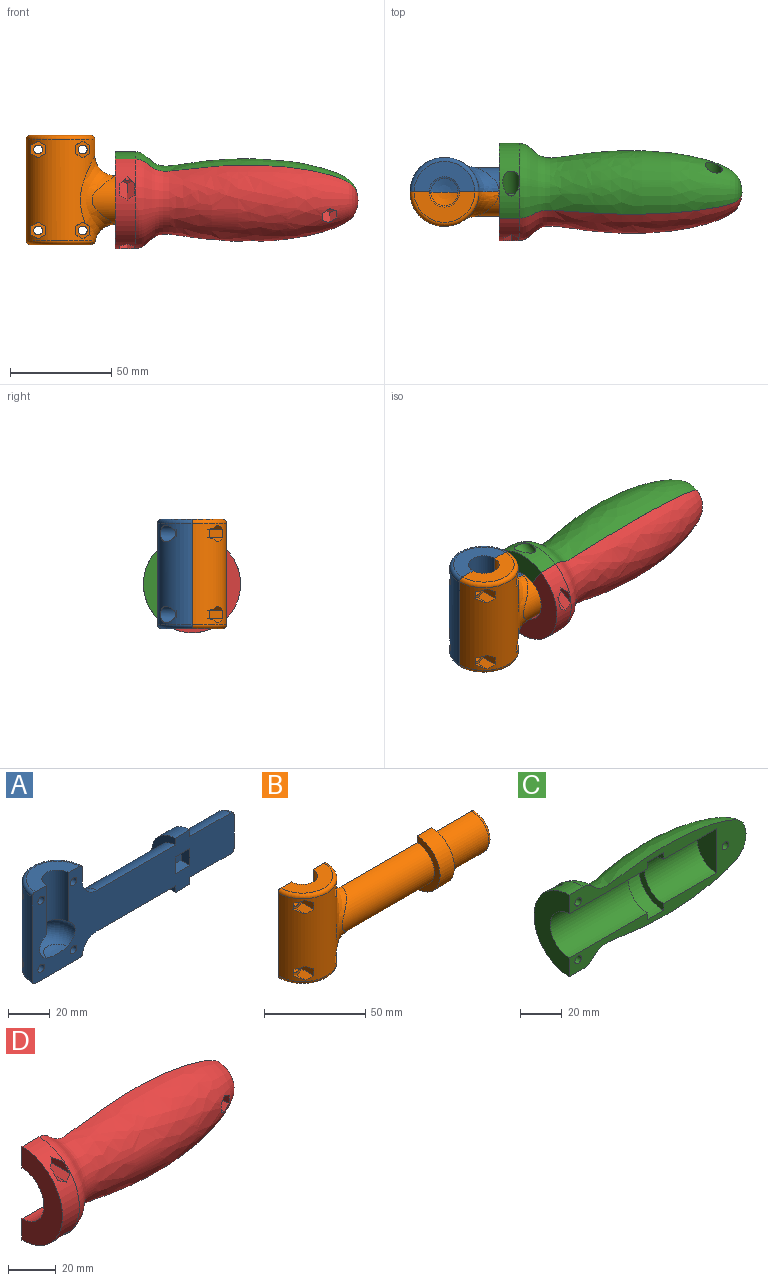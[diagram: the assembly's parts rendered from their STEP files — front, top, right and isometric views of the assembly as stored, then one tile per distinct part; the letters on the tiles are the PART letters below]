
ASSEMBLY  parts=4 mates=3
PART A: 35 faces, bbox 139.5x21.6x55.1 mm
  f0: cylinder r=17mm len=50mm, axis (0,0,1), area 1879.9mm2, adj f2,f12,f19,f20,f22,f23,f24,f25
  f1: cylinder r=2.2mm len=6mm, axis (0,-1,0), area 82.9mm2, adj f12,f28
  f2: bspline ~44.05x17.18mm, area 505.6mm2, adj f0,f11,f12,f18,f25
  f3: cylinder r=2.2mm len=6mm, axis (0,-1,0), area 82.9mm2, adj f12,f29
  f4: cylinder r=2.2mm len=6mm, axis (0,-1,0), area 82.9mm2, adj f12,f26
  f5: cylinder r=2.2mm len=6mm, axis (0,-1,0), area 82.9mm2, adj f12,f27
  f6: plane 20x10mm, normal (1,0,0), area 157.1mm2, adj f12,f21
  f7: cylinder r=12mm len=28mm, axis (-1,0,0), area 1055.6mm2, adj f8,f12,f21
  f8: plane 32x16mm, normal (1,0,0), area 175.9mm2, adj f7,f9,f12
  f9: cylinder r=16mm len=32mm, axis (-1,0,0), area 502.7mm2, adj f8,f10,f12
  f10: plane 32x16mm, normal (-1,0,0), area 175.9mm2, adj f9,f11,f12
  f11: cylinder r=12mm len=53mm, axis (-1,0,0), area 1998.1mm2, adj f2,f10,f12
  f12: plane 138.09x55.09mm, normal (0,-1,0), area 3522.4mm2, adj f0,f1,f2,f3,f4,f5,f6,f7
  f13: plane 30.17x15mm, normal (0,0,-1), area 353.9mm2, adj f12,f18,f19
  f14: plane 30x15mm, normal (0,0,1), area 265.1mm2, adj f12,f17,f20
  f15: sphere r=23mm, area 69.8mm2, adj f12,f16
  f16: torus R=4.53mm, axis (0,0,1), area 587.6mm2, adj f12,f15,f17
  f17: cylinder r=7.5mm len=29mm, axis (0,0,1), area 683.3mm2, adj f12,f14,f16
  f18: bspline ~9.18x3.75mm, area 16.5mm2, adj f2,f12,f13,f19
  f19: torus R=15mm, axis (0,0,-1), area 142.9mm2, adj f0,f12,f13,f18
  f20: torus R=15mm, axis (0,0,1), area 160.6mm2, adj f0,f12,f14
  f21: torus R=10mm, axis (1,0,0), area 111.3mm2, adj f6,f7,f12
  f22: cylinder r=4mm len=8mm, axis (0,1,0), area 115mm2, adj f0,f27
  f23: cylinder r=4mm len=8mm, axis (0,1,0), area 115mm2, adj f0,f26
  f24: cylinder r=4mm len=8mm, axis (0,1,0), area 115mm2, adj f0,f29
  f25: cylinder r=4mm len=8mm, axis (0,1,0), area 117.1mm2, adj f0,f2,f28
  f26: cone r=2.2mm half-angle=45deg, axis (0,1,0), area 49.6mm2, adj f4,f23
  f27: cone r=2.2mm half-angle=45deg, axis (0,1,0), area 49.6mm2, adj f5,f22
  f28: cone r=2.2mm half-angle=45deg, axis (0,1,0), area 49.6mm2, adj f1,f25
  f29: cone r=2.2mm half-angle=45deg, axis (0,1,0), area 49.6mm2, adj f3,f24
  f30: plane 10x6mm, normal (1,0,0), area 60mm2, adj f12,f31,f33,f34
  f31: plane 10x6mm, normal (0,0,1), area 60mm2, adj f12,f30,f32,f34
  f32: plane 10x6mm, normal (-1,0,0), area 60mm2, adj f12,f31,f33,f34
  f33: plane 10x6mm, normal (0,0,-1), area 60mm2, adj f12,f30,f32,f34
  f34: plane 10x10mm, normal (0,-1,0), area 100mm2, adj f30,f31,f32,f33
PART B: 55 faces, bbox 139.5x20.9x55.1 mm
  f0: cylinder r=2.2mm len=7mm, axis (0,1,0), area 96.8mm2, adj f11,f23
  f1: cylinder r=2.2mm len=7mm, axis (0,1,0), area 96.8mm2, adj f11,f30
  f2: cylinder r=2.2mm len=7mm, axis (0,1,0), area 96.8mm2, adj f11,f44
  f3: cylinder r=2.2mm len=7mm, axis (0,1,0), area 96.8mm2, adj f11,f37
  f4: cylinder r=17mm len=50mm, axis (0,0,1), area 1906.5mm2, adj f11,f17,f18,f19,f20,f21,f22,f24
  f5: plane 20x10mm, normal (1,0,0), area 157.1mm2, adj f11,f49
  f6: cylinder r=12mm len=28mm, axis (-1,0,0), area 1055.6mm2, adj f7,f11,f49
  f7: plane 32x16mm, normal (1,0,0), area 175.9mm2, adj f6,f8,f11
  f8: cylinder r=16mm len=32mm, axis (-1,0,0), area 502.7mm2, adj f7,f9,f11
  f9: plane 32x16mm, normal (-1,0,0), area 175.9mm2, adj f8,f10,f11
  f10: cylinder r=12mm len=53mm, axis (-1,0,0), area 1998.1mm2, adj f9,f11,f45
  f11: plane 138.09x55.09mm, normal (0,1,0), area 3522.4mm2, adj f0,f1,f2,f3,f4,f5,f6,f7
  f12: plane 30.17x15mm, normal (0,0,-1), area 353.9mm2, adj f11,f46,f47
  f13: plane 30x15mm, normal (0,0,1), area 265.1mm2, adj f11,f16,f48
  f14: sphere r=23mm, area 69.8mm2, adj f11,f15
  f15: torus R=4.53mm, axis (0,0,1), area 587.6mm2, adj f11,f14,f16
  f16: cylinder r=7.5mm len=29mm, axis (0,0,1), area 683.3mm2, adj f11,f13,f15
  f17: plane 6.16x3.8mm, normal (-0.5,0,-0.87), area 16.9mm2, adj f4,f18,f22,f23
  f18: plane 8.39x3.69mm, normal (0.5,0,-0.87), area 30.1mm2, adj f4,f17,f19,f23
  f19: plane 8.31x4.16mm, normal (1,0,0), area 34.5mm2, adj f4,f18,f20,f23
  f20: plane 8.39x3.69mm, normal (0.5,0,0.87), area 30.1mm2, adj f4,f19,f21,f23
  f21: plane 6.16x3.8mm, normal (-0.5,0,0.87), area 16.9mm2, adj f4,f20,f22,f23
  f22: plane 4.16x1.71mm, normal (-1,0,0), area 7.1mm2, adj f4,f17,f21,f23
  f23: plane 8.31x7.2mm, normal (0,-1,0), area 29.7mm2, adj f0,f17,f18,f19,f20,f21,f22
  f24: plane 8.39x3.69mm, normal (-0.5,0,-0.87), area 30.1mm2, adj f4,f25,f29,f30
  f25: plane 6.16x3.8mm, normal (0.5,0,-0.87), area 16.9mm2, adj f4,f24,f26,f30
  f26: plane 4.16x1.71mm, normal (1,0,0), area 7.1mm2, adj f4,f25,f27,f30
  f27: plane 6.16x3.8mm, normal (0.5,0,0.87), area 16.9mm2, adj f4,f26,f28,f30
  f28: plane 8.39x3.69mm, normal (-0.5,0,0.87), area 30.1mm2, adj f4,f27,f29,f30
  f29: plane 8.31x4.16mm, normal (-1,0,0), area 34.5mm2, adj f4,f24,f28,f30
  f30: plane 8.31x7.2mm, normal (0,-1,0), area 29.7mm2, adj f1,f24,f25,f26,f27,f28,f29
  f31: plane 8.39x3.69mm, normal (-0.5,0,-0.87), area 30.1mm2, adj f4,f32,f36,f37
  f32: plane 6.16x3.8mm, normal (0.5,0,-0.87), area 16.9mm2, adj f4,f31,f33,f37
  f33: plane 4.16x1.71mm, normal (1,0,0), area 7.1mm2, adj f4,f32,f34,f37
  f34: plane 6.16x3.8mm, normal (0.5,0,0.87), area 16.9mm2, adj f4,f33,f35,f37
  f35: plane 8.39x3.69mm, normal (-0.5,0,0.87), area 30.1mm2, adj f4,f34,f36,f37
  f36: plane 8.31x4.16mm, normal (-1,0,0), area 34.5mm2, adj f4,f31,f35,f37
  f37: plane 8.31x7.2mm, normal (0,-1,0), area 29.7mm2, adj f3,f31,f32,f33,f34,f35,f36
  f38: plane 5.98x3.62mm, normal (-0.5,0,-0.87), area 17.5mm2, adj f4,f39,f43,f44,f45
  f39: plane 8.39x3.69mm, normal (0.5,0,-0.87), area 30.1mm2, adj f4,f38,f40,f44
  f40: plane 8.31x4.16mm, normal (1,0,0), area 34.5mm2, adj f4,f39,f41,f44
  f41: plane 8.39x3.69mm, normal (0.5,0,0.87), area 30.1mm2, adj f4,f40,f42,f44
  f42: plane 6.16x3.8mm, normal (-0.5,0,0.87), area 16.9mm2, adj f4,f41,f43,f44,f45
  f43: plane 4.16x2.33mm, normal (-1,0,0), area 8.1mm2, adj f38,f42,f44,f45
  f44: plane 8.31x7.2mm, normal (0,-1,0), area 29.7mm2, adj f2,f38,f39,f40,f41,f42,f43
  f45: bspline ~44.01x17.16mm, area 495.9mm2, adj f4,f10,f11,f38,f42,f43,f46
  f46: bspline ~9.18x3.75mm, area 16.5mm2, adj f11,f12,f45,f47
  f47: torus R=15mm, axis (0,0,-1), area 142.9mm2, adj f4,f11,f12,f46
  f48: torus R=15mm, axis (0,0,1), area 160.6mm2, adj f4,f11,f13
  f49: torus R=10mm, axis (1,0,0), area 111.3mm2, adj f5,f6,f11
  f50: plane 10x6mm, normal (-1,0,0), area 60mm2, adj f11,f51,f53,f54
  f51: plane 10x6mm, normal (0,0,1), area 60mm2, adj f11,f50,f52,f54
  f52: plane 10x6mm, normal (1,0,0), area 60mm2, adj f11,f51,f53,f54
  f53: plane 10x6mm, normal (0,0,-1), area 60mm2, adj f11,f50,f52,f54
  f54: plane 10x10mm, normal (0,1,0), area 100mm2, adj f50,f51,f52,f53
PART C: 19 faces, bbox 120x24x48 mm
  f0: revolved ~110x48mm, area 6482.1mm2, adj f1,f12,f13,f14,f15
  f1: cylinder r=24mm len=48mm, axis (-1,0,0), area 588.8mm2, adj f0,f5,f12,f14,f15
  f2: cylinder r=2.2mm len=5.05mm, axis (0,-1,0), area 69.8mm2, adj f12,f17
  f3: cylinder r=2.2mm len=5.05mm, axis (0,-1,0), area 69.8mm2, adj f12,f16
  f4: cylinder r=2.2mm len=5.05mm, axis (0,-1,0), area 69.8mm2, adj f12,f18
  f5: plane 48x24mm, normal (-1,0,0), area 639.3mm2, adj f1,f6,f12
  f6: cylinder r=13mm len=53mm, axis (-1,0,0), area 2164.6mm2, adj f5,f7,f12
  f7: plane 34x17mm, normal (1,0,0), area 188.5mm2, adj f6,f8,f12
  f8: cylinder r=17mm len=34mm, axis (-1,0,0), area 587.5mm2, adj f7,f9,f12
  f9: plane 34x17mm, normal (-1,0,0), area 188.5mm2, adj f8,f10,f12
  f10: cylinder r=13mm len=36mm, axis (-1,0,0), area 1470.3mm2, adj f9,f11,f12
  f11: plane 26x13mm, normal (-1,0,0), area 265.5mm2, adj f10,f12
  f12: plane 120.02x48.02mm, normal (0,-1,0), area 1711.8mm2, adj f0,f1,f2,f3,f4,f5,f6,f7
  f13: cylinder r=4.25mm len=8.91mm, axis (0,1,0), area 192.6mm2, adj f0,f18
  f14: cylinder r=4.25mm len=13.23mm, axis (0,1,0), area 247.3mm2, adj f0,f1,f17
  f15: cylinder r=4.25mm len=13.23mm, axis (0,1,0), area 247.3mm2, adj f0,f1,f16
  f16: cone r=2.15mm half-angle=45deg, axis (0,1,0), area 58.7mm2, adj f3,f15
  f17: cone r=2.15mm half-angle=45deg, axis (0,1,0), area 58.7mm2, adj f2,f14
  f18: cone r=2.15mm half-angle=45deg, axis (0,1,0), area 58.7mm2, adj f4,f13
PART D: 34 faces, bbox 120.1x24.1x48.1 mm
  f0: cylinder r=2.2mm len=5mm, axis (0,1,0), area 69.1mm2, adj f12,f26
  f1: cylinder r=2.2mm len=5mm, axis (0,1,0), area 69.1mm2, adj f12,f19
  f2: cylinder r=2.2mm len=5mm, axis (0,1,0), area 69.1mm2, adj f12,f33
  f3: revolved ~110x48mm, area 6495.4mm2, adj f4,f12,f27,f28,f29,f30,f31,f32
  f4: cylinder r=24mm len=48mm, axis (-1,0,0), area 623.4mm2, adj f3,f5,f12,f13,f14,f15,f16,f17
  f5: plane 48x24mm, normal (-1,0,0), area 639.3mm2, adj f4,f6,f12
  f6: cylinder r=13mm len=53mm, axis (-1,0,0), area 2164.6mm2, adj f5,f7,f12
  f7: plane 34x17mm, normal (1,0,0), area 188.5mm2, adj f6,f8,f12
  f8: cylinder r=17mm len=34mm, axis (-1,0,0), area 587.5mm2, adj f7,f9,f12
  f9: plane 34x17mm, normal (-1,0,0), area 188.5mm2, adj f8,f10,f12
  f10: cylinder r=13mm len=36mm, axis (-1,0,0), area 1470.3mm2, adj f9,f11,f12
  f11: plane 26x13mm, normal (-1,0,0), area 265.5mm2, adj f10,f12
  f12: plane 120.02x48.02mm, normal (0,1,0), area 1711.8mm2, adj f0,f1,f2,f3,f4,f5,f6,f7
  f13: plane 15.34x3.67mm, normal (-0.5,0,-0.87), area 60.5mm2, adj f4,f14,f18,f19
  f14: plane 15.34x3.67mm, normal (0.5,0,-0.87), area 60.5mm2, adj f4,f13,f15,f19
  f15: plane 13.8x4.16mm, normal (1,0,0), area 49.3mm2, adj f4,f14,f16,f19
  f16: plane 9.56x3.6mm, normal (0.5,0,0.87), area 33.4mm2, adj f4,f15,f17,f19
  f17: plane 9.56x3.6mm, normal (-0.5,0,0.87), area 33.4mm2, adj f4,f16,f18,f19
  f18: plane 13.8x4.16mm, normal (-1,0,0), area 49.3mm2, adj f4,f13,f17,f19
  f19: plane 8.31x7.2mm, normal (0,-1,0), area 29.7mm2, adj f1,f13,f14,f15,f16,f17,f18
  f20: plane 9.56x3.6mm, normal (-0.5,0,-0.87), area 33.4mm2, adj f4,f21,f25,f26
  f21: plane 9.56x3.6mm, normal (0.5,0,-0.87), area 33.4mm2, adj f4,f20,f22,f26
  f22: plane 13.8x4.16mm, normal (1,0,0), area 49.3mm2, adj f4,f21,f23,f26
  f23: plane 15.34x3.67mm, normal (0.5,0,0.87), area 60.5mm2, adj f4,f22,f24,f26
  f24: plane 15.34x3.67mm, normal (-0.5,0,0.87), area 60.5mm2, adj f4,f23,f25,f26
  f25: plane 13.8x4.16mm, normal (-1,0,0), area 49.3mm2, adj f4,f20,f24,f26
  f26: plane 8.31x7.2mm, normal (0,-1,0), area 29.7mm2, adj f0,f20,f21,f22,f23,f24,f25
  f27: plane 9.11x3.6mm, normal (-0.5,0,-0.87), area 36.1mm2, adj f3,f28,f32,f33
  f28: plane 10.69x3.6mm, normal (0.5,0,-0.87), area 41.3mm2, adj f3,f27,f29,f33
  f29: plane 10.83x4.16mm, normal (1,0,0), area 44.8mm2, adj f3,f28,f30,f33
  f30: plane 10.69x3.6mm, normal (0.5,0,0.87), area 41.3mm2, adj f3,f29,f31,f33
  f31: plane 9.11x3.6mm, normal (-0.5,0,0.87), area 36.1mm2, adj f3,f30,f32,f33
  f32: plane 8.36x4.16mm, normal (-1,0,0), area 34.5mm2, adj f3,f27,f31,f33
  f33: plane 8.31x7.2mm, normal (0,-1,0), area 29.7mm2, adj f2,f27,f28,f29,f30,f31,f32
PLACE A at identity
PLACE B at identity fixed
PLACE C rot(axis=(1,0,0),32.5deg) t=(27,0,0)mm
PLACE D rot(axis=(1,0,0),32.5deg) t=(27,0,0)mm
MATE fastened D.f0 <-> C.f2  axis (0,0.84,0.54) through (33,-9.14,14.33)mm
MATE revolute D.f4 <-> B.f6  axis (1,0,0) through (80,0,0)mm
MATE fastened B.f1 <-> A.f4  axis (0,1,0) through (-11,0,25)mm
